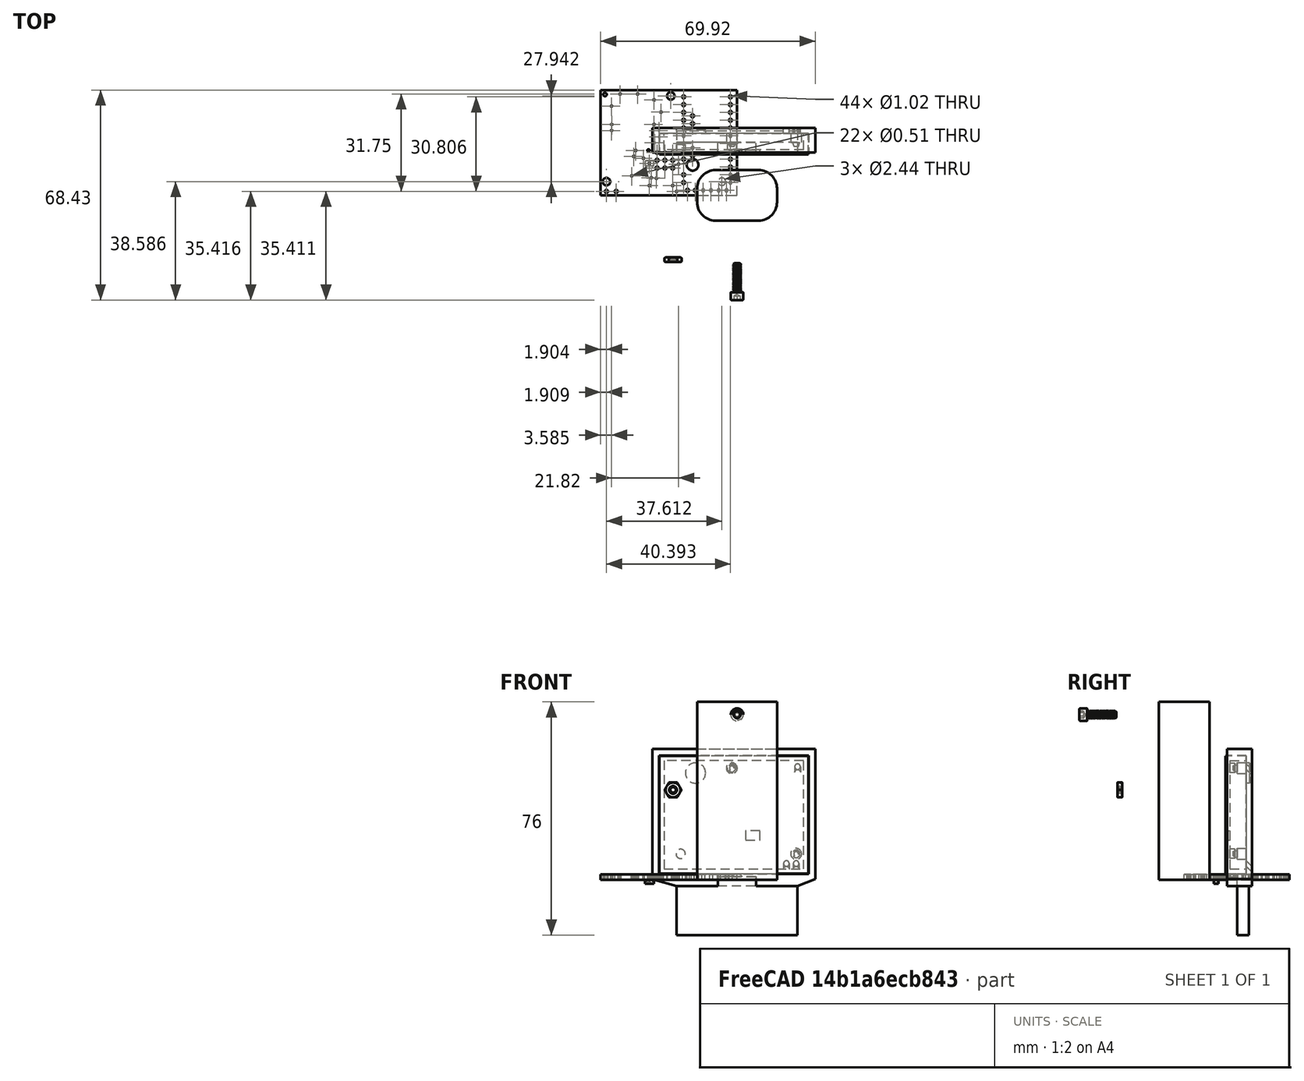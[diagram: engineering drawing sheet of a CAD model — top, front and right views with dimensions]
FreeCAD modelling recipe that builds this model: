
FCSTD DOCUMENT  (FreeCAD 1.0R39109 (Git))
Label: Placement
License: All rights reserved
LicenseURL: https://en.wikipedia.org/wiki/All_rights_reserved
objects: Sketcher::SketchObject×17, PartDesign::Pad×11, PartDesign::Point×11, PartDesign::Plane×6, Part::Feature×5, PartDesign::Pocket×5, PartDesign::SubShapeBinder×4, Mesh::Feature×4, App::Part×3, PartDesign::Body×3
note: 111 computed .brp shape members not serialized (recipe doc carries the construction recipe); baked Part::Feature solids carry a one-line shape summary decoded from their .brp

FEATURE [Part::Feature] Part__Feature006  label="pcb"
  Placement = pos=(0,0,0) rot=(0,0,1;1.5708rad)
  shape: bbox 44.45 x 34.29 x 1.778 mm, 78 faces (baked)
FEATURE [Part::Feature] Part__Feature007  label="SOT23"
  Placement = pos=(-28.5698,10.3914,0) rot=(0,1,0;3.14159rad)
  shape: bbox 2.9 x 2.134 x 1.25 mm, 27 faces (baked)
FEATURE [App::Part] pcb  label="pcb001"
  Group = -> [Part__Feature006,Part__Feature007]
  Origin = -> Origin001
  Placement = pos=(-23.3,15.5,4) rot=(0,0.707107,0.707107;3.14159rad)
FEATURE [Sketcher::SketchObject] Sketch
  ArcFitTolerance = 1e-06
  AttachmentSupport = -> [XY_Plane003]
  FullyConstrained = true
  MakeInternals = false
  MapMode = 5
  sketch-geometry (13):
    g0: LineSegment StartX=13 StartY=-2.25 StartZ=0 EndX=13 EndY=2.25 EndZ=0
    g1: LineSegment StartX=7 StartY=8.25 StartZ=0 EndX=-7 EndY=8.25 EndZ=0
    g2: LineSegment StartX=-13 StartY=2.25 StartZ=0 EndX=-13 EndY=-2.25 EndZ=0
    g3: LineSegment StartX=-7 StartY=-8.25 StartZ=0 EndX=7 EndY=-8.25 EndZ=0
    g4: GeomPoint [constr] X=0 Y=0 Z=0
    g5: ArcOfCircle CenterX=-7 CenterY=2.25 CenterZ=0 NormalX=0 NormalY=0 NormalZ=1 AngleXU=0 Radius=6 StartAngle=1.5708 EndAngle=3.14159
    g6: GeomPoint [constr] X=-13 Y=8.25 Z=0
    g7: ArcOfCircle CenterX=7 CenterY=2.25 CenterZ=0 NormalX=0 NormalY=0 NormalZ=1 AngleXU=0 Radius=6 StartAngle=7e-15 EndAngle=1.5708
    g8: GeomPoint [constr] X=13 Y=8.25 Z=0
    g9: ArcOfCircle CenterX=7 CenterY=-2.25 CenterZ=0 NormalX=0 NormalY=0 NormalZ=1 AngleXU=0 Radius=6 StartAngle=4.71239 EndAngle=6.28319
    g10: GeomPoint [constr] X=13 Y=-8.25 Z=0
    g11: ArcOfCircle CenterX=-7 CenterY=-2.25 CenterZ=0 NormalX=0 NormalY=0 NormalZ=1 AngleXU=0 Radius=6 StartAngle=3.14159 EndAngle=4.71239
    g12: GeomPoint [constr] X=-13 Y=-8.25 Z=0
  constraints (28):
    c: Vertical(g0)
    c: Vertical(g2)
    c: Horizontal(g1)
    c: Horizontal(g3)
    c: Symmetric(g6,g10,g4)
    c: Coincident(g4,g-1)
    c: DistanceY(g12,g6) = 16.5
    c: DistanceX(g6,g8) = 26
    c: PointOnObject(g6,g1)
    c: PointOnObject(g6,g2)
    c: Tangent(g1,g5) = -1.5708
    c: Tangent(g2,g5) = -1.5708
    c: PointOnObject(g8,g1)
    c: PointOnObject(g8,g0)
    c: Tangent(g1,g7) = -1.5708
    c: Tangent(g0,g7) = -1.5708
    c: PointOnObject(g10,g0)
    c: PointOnObject(g10,g3)
    c: Tangent(g0,g9) = -1.5708
    c: Tangent(g3,g9) = -1.5708
    c: PointOnObject(g12,g3)
    c: PointOnObject(g12,g2)
    c: Tangent(g3,g11) = -1.5708
    c: Tangent(g2,g11) = -1.5708
    c: Equal(g5,g11)
    c: Equal(g11,g9)
    c: Equal(g11,g7)
    c: Radius(g7) = 6
FEATURE [PartDesign::Pad] Pad
  Direction = (0,0,1)
  Length = 58
  Length2 = 10
  Profile = -> Sketch
  ReferenceAxis = -> Sketch [N_Axis]
  Refine = true
  Suppressed = false
  Type = 0
FEATURE [PartDesign::Body] Body
  AllowCompound = false
  Group = -> [Sketch,Pad]
  Origin = -> Origin003
  Tip = -> Pad
FEATURE [App::Part] Part001  label="AA holder"
  Group = -> [Body]
  Origin = -> Origin002
  Placement = pos=(0,-35.5,-12) rot=(0,0,1;0rad)
FEATURE [Part::Feature] Part__Feature  label="Num 3 socket head"
  Placement = pos=(0,-22.098,53.848) rot=(1,0,0;1.5708rad)
  shape: bbox 4.09 x 12.24 x 4.09 mm, 70 faces (baked)
FEATURE [Part::Feature] Part__Feature008  label="num 3 nut"
  Placement = pos=(-20.85,-21,29.3) rot=(0,1,0;0.523599rad)
  shape: bbox 5.5 x 2.051 x 5.5 mm, 38 faces (baked)
FEATURE [PartDesign::SubShapeBinder] Binder
  BindCopyOnChange = 0
  BindMode = 0
  ClaimChildren = false
  Context = -> Part [Body001.Binder.]
  Fuse = false
  MakeFace = true
  OffsetFill = false
  OffsetIntersection = false
  OffsetJoinType = 0
  OffsetOpenResult = false
  PartialLoad = false
  Refine = true
  Relative = true
  Support = -> [pcb[Part__Feature006.]]
  _Version = 2
FEATURE [PartDesign::SubShapeBinder] Binder001
  BindCopyOnChange = 0
  BindMode = 0
  ClaimChildren = false
  Context = -> Part [Body001.Binder001.]
  Fuse = false
  MakeFace = true
  OffsetFill = false
  OffsetIntersection = false
  OffsetJoinType = 0
  OffsetOpenResult = false
  PartialLoad = false
  Refine = true
  Relative = true
  Support = -> [pcb[Part__Feature007.]]
  _Version = 2
FEATURE [PartDesign::Plane] DatumPlane  label="enclosure face PCB"
  AttachmentOffset = pos=(0,0,0.635) rot=(0,0,1;0rad)
  AttachmentSupport = -> [Binder]
  Length = 61.8227
  MapMode = 5
  Placement = pos=(0,14.865,1e-16) rot=(1,0,0;1.5708rad)
  ResizeMode = 0
  Width = 76.8127
FEATURE [PartDesign::Plane] DatumPlane001  label="sensor face"
  AttachmentSupport = -> [Binder001]
  Length = 76.8127
  MapMode = 11
  Placement = pos=(5.26981,14.25,14.3914) rot=(0.57735,0.57735,0.57735;4.18879rad)
  ResizeMode = 0
  Width = 61.8227
FEATURE [Sketcher::SketchObject] Sketch001
  ArcFitTolerance = 1e-06
  AttachmentSupport = -> [DatumPlane]
  ExternalGeometry = -> [Binder]
  FullyConstrained = true
  MakeInternals = false
  MapMode = 5
  Placement = pos=(0,14.865,1e-16) rot=(1,0,0;1.5708rad)
  sketch-geometry (4):
    g0: LineSegment StartX=-25.332 StartY=40.322 StartZ=0 EndX=-25.332 EndY=1.968 EndZ=0
    g1: LineSegment StartX=-25.332 StartY=1.968 StartZ=0 EndX=23.182 EndY=1.968 EndZ=0
    g2: LineSegment StartX=23.182 StartY=1.968 StartZ=0 EndX=23.182 EndY=40.322 EndZ=0
    g3: LineSegment StartX=23.182 StartY=40.322 StartZ=0 EndX=-25.332 EndY=40.322 EndZ=0
  constraints (12):
    c: Coincident(g0,g1)
    c: Coincident(g1,g2)
    c: Coincident(g2,g3)
    c: Coincident(g3,g0)
    c: Vertical(g0)
    c: Vertical(g2)
    c: Horizontal(g1)
    c: Horizontal(g3)
    c: DistanceX(g0,g-3) = 2.032
    c: DistanceX(g-3,g2) = 2.032
    c: DistanceY(g0,g-4) = 2.032
    c: DistanceY(g-3,g2) = 2.032
FEATURE [PartDesign::Pad] Pad001
  Direction = (0,-1,2e-16)
  Length = 1.50012
  Length2 = 10
  Placement = pos=(1.3e-15,14.865,3.6e-15) rot=(1,0,0;1.5708rad)
  Profile = -> Sketch001
  ReferenceAxis = -> Sketch001 [N_Axis]
  Refine = true
  Suppressed = false
  Type = 0
FEATURE [Sketcher::SketchObject] Sketch002
  ArcFitTolerance = 1e-06
  AttachmentSupport = -> [DatumPlane001]
  ExternalGeometry = -> [Binder001]
  FullyConstrained = false
  MakeInternals = false
  MapMode = 5
  Placement = pos=(5.26981,14.25,14.3914) rot=(0.57735,0.57735,0.57735;4.18879rad)
  sketch-geometry (4):
    g0: LineSegment StartX=-1.49114 StartY=2.17791 StartZ=0 EndX=-1.49114 EndY=-2.49451 EndZ=0
    g1: LineSegment StartX=-1.49114 StartY=-2.49451 StartZ=0 EndX=1.64977 EndY=-2.49451 EndZ=0
    g2: LineSegment StartX=1.64977 StartY=-2.49451 StartZ=0 EndX=1.64977 EndY=2.17791 EndZ=0
    g3: LineSegment StartX=1.64977 StartY=2.17791 StartZ=0 EndX=-1.49114 EndY=2.17791 EndZ=0
  constraints (8):
    c: Coincident(g0,g1)
    c: Coincident(g1,g2)
    c: Coincident(g2,g3)
    c: Coincident(g3,g0)
    c: Vertical(g0)
    c: Vertical(g2)
    c: Horizontal(g1)
    c: Horizontal(g3)
FEATURE [PartDesign::Pocket] Pocket
  BaseFeature = -> Pad001
  Direction = (0,-1,0)
  Length = 5
  Length2 = 5
  Placement = pos=(1.3e-15,14.865,3.6e-15) rot=(1,0,0;1.5708rad)
  Profile = -> Sketch002
  ReferenceAxis = -> Sketch002 [N_Axis]
  Refine = true
  Reversed = true
  Suppressed = false
  Type = 1
FEATURE [Sketcher::SketchObject] Sketch003
  ArcFitTolerance = 1e-06
  AttachmentSupport = -> [DatumPlane]
  ExternalGeometry = -> [Pocket]
  FullyConstrained = true
  MakeInternals = false
  MapMode = 5
  Placement = pos=(0,14.865,1e-16) rot=(1,0,0;1.5708rad)
  sketch-geometry (10):
    g0: LineSegment StartX=23.182 StartY=40.322 StartZ=0 EndX=-25.332 EndY=40.322 EndZ=0
    g1: LineSegment StartX=-25.332 StartY=40.322 StartZ=0 EndX=-25.332 EndY=1.968 EndZ=0
    g2: LineSegment StartX=-25.332 StartY=1.968 StartZ=0 EndX=23.182 EndY=1.968 EndZ=0
    g3: LineSegment StartX=23.182 StartY=1.968 StartZ=0 EndX=23.182 EndY=40.322 EndZ=0
    g4: LineSegment StartX=21.658 StartY=38.798 StartZ=0 EndX=-23.808 EndY=38.798 EndZ=0
    g5: LineSegment StartX=-23.808 StartY=38.798 StartZ=0 EndX=-23.808 EndY=3.492 EndZ=0
    g6: LineSegment StartX=-23.808 StartY=3.492 StartZ=0 EndX=21.658 EndY=3.492 EndZ=0
    g7: LineSegment StartX=21.658 StartY=3.492 StartZ=0 EndX=21.658 EndY=38.798 EndZ=0
    g8: LineSegment [constr] StartX=-1.075 StartY=38.798 StartZ=0 EndX=-1.075 EndY=40.322 EndZ=0
    g9: LineSegment [constr] StartX=21.658 StartY=21.145 StartZ=0 EndX=23.182 EndY=21.145 EndZ=0
  constraints (26):
    c: Coincident(g0,g1)
    c: Coincident(g1,g2)
    c: Coincident(g2,g3)
    c: Coincident(g3,g0)
    c: Horizontal(g0)
    c: Horizontal(g2)
    c: Vertical(g1)
    c: Vertical(g3)
    c: Coincident(g0,g-3)
    c: Coincident(g1,g-4)
    c: Coincident(g4,g5)
    c: Coincident(g5,g6)
    c: Coincident(g6,g7)
    c: Coincident(g7,g4)
    c: Horizontal(g4)
    c: Horizontal(g6)
    c: Vertical(g5)
    c: Vertical(g7)
    c: Symmetric(g4,g4,g8)
    c: Symmetric(g0,g0,g8)
    c: Vertical(g8)
    c: Symmetric(g7,g7,g9)
    c: Symmetric(g3,g3,g9)
    c: Horizontal(g9)
    c: Equal(g9,g8)
    c: DistanceY(g8,g8) = 1.524
FEATURE [PartDesign::Pad] Pad002
  BaseFeature = -> Pocket
  Direction = (0,-1,2e-16)
  Length = 5.334
  Length2 = 10
  Placement = pos=(1.3e-15,14.865,3.6e-15) rot=(1,0,0;1.5708rad)
  Profile = -> Sketch003
  ReferenceAxis = -> Sketch003 [N_Axis]
  Refine = true
  Reversed = true
  Suppressed = false
  Type = 0
FEATURE [Part::Feature] Pluviometer_base_pts
  shape: bbox 120 x 120 x 80 mm, 0 faces, 0 solids (baked)
FEATURE [PartDesign::Plane] DatumPlane002
  AttachmentSupport = -> [Pluviometer_base_pts]
  Length = 65.0694
  MapMode = 13
  Placement = pos=(6.66667,21,-7.33333) rot=(0,0.707107,0.707107;3.14159rad)
  ResizeMode = 0
  Width = 79.6104
FEATURE [PartDesign::Point] DatumPoint
  AttacherType = Attacher::AttachEnginePoint
  AttachmentSupport = -> [Pluviometer_base_pts]
  MapMode = 37
  Placement = pos=(20,17,-18) rot=(0,0,1;0rad)
FEATURE [PartDesign::Point] DatumPoint001
  AttacherType = Attacher::AttachEnginePoint
  AttachmentSupport = -> [Pluviometer_base_pts]
  MapMode = 37
  Placement = pos=(20,17,-18) rot=(0,0,1;0rad)
FEATURE [PartDesign::Point] DatumPoint002
  AttacherType = Attacher::AttachEnginePoint
  AttachmentSupport = -> [Pluviometer_base_pts]
  MapMode = 37
  Placement = pos=(-20,17,-18) rot=(0,0,1;0rad)
FEATURE [PartDesign::Point] DatumPoint003
  AttacherType = Attacher::AttachEnginePoint
  AttachmentSupport = -> [Pluviometer_base_pts]
  MapMode = 37
  Placement = pos=(-20,21,-2) rot=(0,0,1;0rad)
FEATURE [PartDesign::Point] DatumPoint004
  AttacherType = Attacher::AttachEnginePoint
  AttachmentSupport = -> [Pluviometer_base_pts]
  MapMode = 37
  Placement = pos=(-20,21,-2) rot=(0,0,1;0rad)
FEATURE [PartDesign::Point] DatumPoint005
  AttacherType = Attacher::AttachEnginePoint
  AttachmentSupport = -> [Pluviometer_base_pts]
  MapMode = 37
  Placement = pos=(20,21,-2) rot=(0,0,1;0rad)
FEATURE [Sketcher::SketchObject] Sketch004
  ArcFitTolerance = 1e-06
  AttachmentSupport = -> [DatumPlane002]
  ExternalGeometry = -> [DatumPoint005,DatumPoint003,DatumPoint002,DatumPoint]
  FullyConstrained = true
  MakeInternals = false
  MapMode = 5
  Placement = pos=(6.66667,21,-7.33333) rot=(0,0.707107,0.707107;3.14159rad)
  sketch-geometry (4):
    g0: LineSegment StartX=-13.0333 StartY=5.33333 StartZ=0 EndX=-13.0333 EndY=-10.6667 EndZ=0
    g1: LineSegment StartX=-13.0333 StartY=-10.6667 StartZ=0 EndX=26.3667 EndY=-10.6667 EndZ=0
    g2: LineSegment StartX=26.3667 StartY=-10.6667 StartZ=0 EndX=26.3667 EndY=5.33333 EndZ=0
    g3: LineSegment StartX=26.3667 StartY=5.33333 StartZ=0 EndX=-13.0333 EndY=5.33333 EndZ=0
  constraints (12):
    c: Coincident(g0,g1)
    c: Coincident(g1,g2)
    c: Coincident(g2,g3)
    c: Coincident(g3,g0)
    c: Vertical(g0)
    c: Vertical(g2)
    c: Horizontal(g1)
    c: Horizontal(g3)
    c: Horizontal(g0,g-3)
    c: Horizontal(g-6,g0)
    c: DistanceX(g-3,g0) = 0.3
    c: DistanceX(g2,g-4) = 0.3
FEATURE [PartDesign::Pad] Pad003
  Direction = (0,1,-2e-16)
  Length = 3.75
  Length2 = 10
  Placement = pos=(6.66667,21,-7.33333) rot=(0,0.707107,0.707107;3.14159rad)
  Profile = -> Sketch004
  ReferenceAxis = -> Sketch004 [N_Axis]
  Refine = true
  Reversed = true
  Suppressed = false
  Type = 0
FEATURE [PartDesign::SubShapeBinder] Binder002
  BindCopyOnChange = 0
  BindMode = 0
  ClaimChildren = false
  Context = -> Part [Body002.Binder002.]
  Fuse = false
  MakeFace = true
  OffsetFill = false
  OffsetIntersection = false
  OffsetJoinType = 0
  OffsetOpenResult = false
  PartialLoad = false
  Refine = true
  Relative = true
  Support = -> [Body001]
  _Version = 2
FEATURE [Sketcher::SketchObject] Sketch005
  ArcFitTolerance = 1e-06
  AttachmentSupport = -> [DatumPlane002]
  ExternalGeometry = -> [Binder002,Pad003]
  FullyConstrained = false
  MakeInternals = false
  MapMode = 5
  Placement = pos=(6.66667,21,-7.33333) rot=(0,0.707107,0.707107;3.14159rad)
  sketch-geometry (8):
    g0: LineSegment StartX=-13.0333 StartY=5.33333 StartZ=0 EndX=-13.0333 EndY=-10.6667 EndZ=0
    g1: LineSegment StartX=-13.0333 StartY=-10.6667 StartZ=0 EndX=26.3667 EndY=-10.6667 EndZ=0
    g2: LineSegment StartX=26.3667 StartY=-10.6667 StartZ=0 EndX=26.3667 EndY=5.33333 EndZ=0
    g3: LineSegment StartX=-18.8013 StartY=49.9413 StartZ=0 EndX=-18.8013 EndY=7.52333 EndZ=0
    g4: LineSegment StartX=34.2847 StartY=7.52333 StartZ=0 EndX=34.2847 EndY=49.9413 EndZ=0
    g5: LineSegment StartX=34.2847 StartY=49.9413 StartZ=0 EndX=-18.8013 EndY=49.9413 EndZ=0
    g6: LineSegment StartX=-13.0333 StartY=5.33333 StartZ=0 EndX=-18.8013 EndY=7.52333 EndZ=0
    g7: LineSegment StartX=26.3667 StartY=5.33333 StartZ=0 EndX=34.2847 EndY=7.52333 EndZ=0
  constraints (18):
    c: Coincident(g0,g-6)
    c: Vertical(g0)
    c: Coincident(g1,g0)
    c: Coincident(g1,g-6)
    c: Coincident(g2,g1)
    c: Coincident(g4,g5)
    c: Coincident(g5,g3)
    c: Vertical(g3)
    c: Vertical(g4)
    c: Horizontal(g5)
    c: DistanceX(g3,g-3) = 2.286
    c: DistanceX(g-3,g4) = 2.286
    c: DistanceY(g-3,g3) = 2.286
    c: DistanceY(g3,g-4) = 1.778
    c: Coincident(g6,g0)
    c: Coincident(g6,g3)
    c: Coincident(g7,g2)
    c: Coincident(g7,g4)
FEATURE [PartDesign::Plane] DatumPlane003
  AttachmentSupport = -> [Binder002]
  Length = 65.0694
  MapMode = 13
  Placement = pos=(6.50267,20.199,15.2607) rot=(1,0,0;1.5708rad)
  ResizeMode = 0
  Width = 79.6104
FEATURE [PartDesign::Pad] Pad004
  BaseFeature = -> Pad003
  Direction = (0,1,-2e-16)
  Length = 10
  Length2 = 10
  Placement = pos=(6.66667,21,-7.33333) rot=(0,0.707107,0.707107;3.14159rad)
  Profile = -> Sketch005
  ReferenceAxis = -> Sketch005 [N_Axis]
  Refine = true
  Suppressed = false
  Type = 3
  UpToFace = -> DatumPlane003
FEATURE [Sketcher::SketchObject] Sketch006
  ArcFitTolerance = 1e-06
  AttachmentSupport = -> [Pad004]
  ExternalGeometry = -> [Binder002,Pad004]
  FullyConstrained = true
  MakeInternals = false
  MapMode = 5
  Placement = pos=(6.66667,20.199,-7.33333) rot=(0,0.707107,-0.707107;3.14159rad)
  sketch-geometry (10):
    g0: LineSegment StartX=-16.6423 StartY=-9.17433 StartZ=0 EndX=-16.6423 EndY=-47.7823 EndZ=0
    g1: LineSegment StartX=-16.6423 StartY=-47.7823 StartZ=0 EndX=32.1257 EndY=-47.7823 EndZ=0
    g2: LineSegment StartX=32.1257 StartY=-47.7823 StartZ=0 EndX=32.1257 EndY=-9.17433 EndZ=0
    g3: LineSegment StartX=32.1257 StartY=-9.17433 StartZ=0 EndX=-16.6423 EndY=-9.17433 EndZ=0
    g4: LineSegment StartX=34.2847 StartY=-7.52333 StartZ=0 EndX=34.2847 EndY=-49.9413 EndZ=0
    g5: LineSegment StartX=34.2847 StartY=-49.9413 StartZ=0 EndX=-18.8013 EndY=-49.9413 EndZ=0
    g6: LineSegment StartX=-18.8013 StartY=-49.9413 StartZ=0 EndX=-18.8013 EndY=-7.52333 EndZ=0
    g7: LineSegment StartX=-18.8013 StartY=-7.52333 StartZ=0 EndX=-13.0333 EndY=-5.33333 EndZ=0
    g8: LineSegment StartX=-13.0333 StartY=-5.33333 StartZ=0 EndX=26.3667 EndY=-5.33333 EndZ=0
    g9: LineSegment StartX=26.3667 StartY=-5.33333 StartZ=0 EndX=34.2847 EndY=-7.52333 EndZ=0
  constraints (24):
    c: Coincident(g0,g1)
    c: Coincident(g1,g2)
    c: Coincident(g2,g3)
    c: Coincident(g3,g0)
    c: Vertical(g0)
    c: Vertical(g2)
    c: Horizontal(g1)
    c: Horizontal(g3)
    c: DistanceX(g0,g-3) = 0.127
    c: DistanceX(g-3,g2) = 0.127
    c: DistanceY(g-3,g2) = 0.127
    c: DistanceY(g1,g-4) = 0.127
    c: Coincident(g4,g-8)
    c: Coincident(g4,g-5)
    c: Coincident(g5,g4)
    c: Coincident(g5,g-5)
    c: Coincident(g6,g5)
    c: Coincident(g6,g-9)
    c: Coincident(g7,g-9)
    c: Coincident(g7,g-6)
    c: Coincident(g8,g-6)
    c: Coincident(g8,g-7)
    c: Coincident(g9,g-7)
    c: Coincident(g9,g4)
FEATURE [Sketcher::SketchObject] Sketch009
  ArcFitTolerance = 1e-06
  AttachmentSupport = -> [Pad002]
  ExternalGeometry = -> [Binder]
  FullyConstrained = true
  MakeInternals = false
  MapMode = 5
  Placement = pos=(1.3e-15,14.865,3.6e-15) rot=(-1,0,0;1.5708rad)
  sketch-geometry (2):
    g0: Circle CenterX=-18.3663 CenterY=-8.44604 CenterZ=0 NormalX=0 NormalY=0 NormalZ=1 AngleXU=0 Radius=1.524
    g1: Circle CenterX=-1.71311 CenterY=-36.3881 CenterZ=0 NormalX=0 NormalY=0 NormalZ=1 AngleXU=0 Radius=1.524
  constraints (4):
    c: Coincident(g0,g-3)
    c: Coincident(g1,g-4)
    c: Diameter(g1) = 3.048
    c: Equal(g0,g1)
FEATURE [PartDesign::Pad] Pad007
  BaseFeature = -> Pad002
  Direction = (0,1,2e-16)
  Length = 1.5875
  Length2 = 10
  Placement = pos=(1.3e-15,14.865,3.6e-15) rot=(1,0,0;1.5708rad)
  Profile = -> Sketch009
  ReferenceAxis = -> Sketch009 [N_Axis]
  Refine = true
  Suppressed = false
  Type = 3
  UpToFace = -> Binder [Face75]
FEATURE [PartDesign::Body] Body001
  AllowCompound = false
  Group = -> [Binder,Binder001,DatumPlane,DatumPlane001,Sketch001,Pad001,Sketch002,Pocket,Sketch003,Pad002,Sketch009,Pad007]
  Origin = -> Origin004
  Tip = -> Pad007
FEATURE [Mesh::Feature] Pluviometer_funnel  label="Pluviometer-funnel"
FEATURE [Mesh::Feature] Pluviometer_AA  label="Pluviometer-AA"
FEATURE [Mesh::Feature] Pluviometer_base  label="Pluviometer-base"
FEATURE [PartDesign::SubShapeBinder] Binder003
  BindCopyOnChange = 0
  BindMode = 0
  ClaimChildren = false
  Context = -> Part [Body002.Binder003.]
  Fuse = false
  MakeFace = true
  OffsetFill = false
  OffsetIntersection = false
  OffsetJoinType = 0
  OffsetOpenResult = false
  PartialLoad = false
  Refine = true
  Relative = true
  Support = -> [pcb]
  _Version = 2
FEATURE [PartDesign::Point] DatumPoint006
  AttacherType = Attacher::AttachEnginePoint
  AttachmentSupport = -> [Pluviometer_base_pts]
  MapMode = 37
  Placement = pos=(6,17,1) rot=(0,0,1;0rad)
FEATURE [PartDesign::Point] DatumPoint007
  AttacherType = Attacher::AttachEnginePoint
  AttachmentSupport = -> [Pluviometer_base_pts]
  MapMode = 37
  Placement = pos=(-6,17,1) rot=(0,0,1;0rad)
FEATURE [PartDesign::Plane] DatumPlane004  label="axle end"
  AttachmentSupport = -> [Pluviometer_base_pts]
  Length = 65.0694
  MapMode = 13
  Placement = pos=(0.362446,15,-0.177299) rot=(0,0.707107,0.707107;3.14159rad)
  ResizeMode = 0
  Width = 79.6104
FEATURE [PartDesign::Point] DatumPoint008  label="axle end circle 1"
  AttacherType = Attacher::AttachEnginePoint
  AttachmentSupport = -> [Pluviometer_base_pts]
  MapMode = 37
  Placement = pos=(1.625,15,0) rot=(0,0,1;0rad)
FEATURE [PartDesign::Point] DatumPoint009  label="axle end circle 2"
  AttacherType = Attacher::AttachEnginePoint
  AttachmentSupport = -> [Pluviometer_base_pts]
  MapMode = 37
  Placement = pos=(-1.625,-15,0) rot=(0,0,1;0rad)
FEATURE [PartDesign::Point] DatumPoint010  label="axle end circle 3"
  AttacherType = Attacher::AttachEnginePoint
  AttachmentSupport = -> [Pluviometer_base_pts]
  MapMode = 37
  Placement = pos=(-0.8125,15,-1.40729) rot=(0,0,1;0rad)
FEATURE [Mesh::Feature] Pluviometer_bucket  label="Pluviometer-bucket"
  Placement = pos=(0,0,0) rot=(0,1,0;0.349066rad)
FEATURE [Sketcher::SketchObject] Sketch014
  ArcFitTolerance = 1e-06
  AttachmentSupport = -> [DatumPlane002]
  ExternalGeometry = -> [Pad004,Sketch005]
  FullyConstrained = true
  MakeInternals = false
  MapMode = 5
  Placement = pos=(6.66667,21,-7.33333) rot=(0,0.707107,0.707107;3.14159rad)
  sketch-geometry (7):
    g0: LineSegment StartX=34.2847 StartY=7.52333 StartZ=0 EndX=34.2847 EndY=49.9413 EndZ=0
    g1: LineSegment StartX=34.2847 StartY=49.9413 StartZ=0 EndX=-18.8013 EndY=49.9413 EndZ=0
    g2: LineSegment StartX=-18.8013 StartY=49.9413 StartZ=0 EndX=-18.8013 EndY=7.52333 EndZ=0
    g3: LineSegment [constr] StartX=-18.8013 StartY=7.52333 StartZ=0 EndX=34.2847 EndY=7.52333 EndZ=0
    g4: LineSegment StartX=-18.8013 StartY=7.52333 StartZ=0 EndX=-13.0333 EndY=5.33333 EndZ=0
    g5: LineSegment StartX=-13.0333 StartY=5.33333 StartZ=0 EndX=26.3667 EndY=5.33333 EndZ=0
    g6: LineSegment StartX=26.3667 StartY=5.33333 StartZ=0 EndX=34.2847 EndY=7.52333 EndZ=0
  constraints (16):
    c: Coincident(g0,g1)
    c: Coincident(g1,g2)
    c: Coincident(g2,g3)
    c: Coincident(g3,g0)
    c: Vertical(g0)
    c: Vertical(g2)
    c: Horizontal(g1)
    c: Horizontal(g3)
    c: Coincident(g0,g-3)
    c: Coincident(g1,g-4)
    c: Coincident(g4,g2)
    c: Coincident(g4,g-5)
    c: Coincident(g5,g4)
    c: Coincident(g5,g-6)
    c: Coincident(g6,g5)
    c: Coincident(g6,g0)
FEATURE [PartDesign::Pad] Pad008
  BaseFeature = -> Pad004
  Direction = (0,1,-2e-16)
  Length = 1.016
  Length2 = 10
  Placement = pos=(6.66667,21,-7.33333) rot=(0,0.707107,0.707107;3.14159rad)
  Profile = -> Sketch014
  ReferenceAxis = -> Sketch014 [N_Axis]
  Refine = true
  Suppressed = false
  Type = 0
FEATURE [PartDesign::Pad] Pad005
  BaseFeature = -> Pad008
  Direction = (0,-1,-2e-16)
  Length = 2
  Length2 = 10
  Placement = pos=(6.66667,21,-7.33333) rot=(0,0.707107,0.707107;3.14159rad)
  Profile = -> Sketch006
  ReferenceAxis = -> Sketch006 [N_Axis]
  Refine = true
  Suppressed = false
  Type = 3
  UpToFace = -> Pad004 [Face1]
FEATURE [Sketcher::SketchObject] Sketch007
  ArcFitTolerance = 1e-06
  AttachmentSupport = -> [Pad005]
  FullyConstrained = false
  MakeInternals = false
  MapMode = 5
  Placement = pos=(6.66667,21,-7.33333) rot=(0,0.707107,0.707107;3.14159rad)
  sketch-geometry (4):
    g0: LineSegment StartX=9.95147 StartY=11.0285 StartZ=0 EndX=30.2715 EndY=11.0285 EndZ=0
    g1: LineSegment StartX=30.2715 StartY=11.0285 StartZ=0 EndX=30.2715 EndY=17.4643 EndZ=0
    g2: LineSegment StartX=30.2715 StartY=17.4643 StartZ=0 EndX=9.95147 EndY=17.4643 EndZ=0
    g3: LineSegment StartX=9.95147 StartY=17.4643 StartZ=0 EndX=9.95147 EndY=11.0285 EndZ=0
  constraints (10):
    c: Coincident(g0,g1)
    c: Coincident(g1,g2)
    c: Coincident(g2,g3)
    c: Coincident(g3,g0)
    c: Horizontal(g0)
    c: Horizontal(g2)
    c: Vertical(g1)
    c: Vertical(g3)
    c: Distance(g1,g3) = 20.32
    c: Coincident(g0,g-3)
FEATURE [Sketcher::SketchObject] Sketch008
  ArcFitTolerance = 1e-06
  ExternalGeometry = -> [Pad005]
  FullyConstrained = true
  MakeInternals = false
  MapMode = 5
  Placement = pos=(6.66667,17.25,-7.33333) rot=(0,0.707107,-0.707107;3.14159rad)
  sketch-geometry (10):
    g0: LineSegment StartX=-13.0333 StartY=-5.33333 StartZ=0 EndX=26.3667 EndY=-5.33333 EndZ=0
    g1: LineSegment StartX=26.3667 StartY=-5.33333 StartZ=0 EndX=34.2847 EndY=-7.52333 EndZ=0
    g2: LineSegment StartX=34.2847 StartY=-7.52333 StartZ=0 EndX=34.2847 EndY=-49.9413 EndZ=0
    g3: LineSegment StartX=34.2847 StartY=-49.9413 StartZ=0 EndX=-18.8013 EndY=-49.9413 EndZ=0
    g4: LineSegment StartX=-18.8013 StartY=-49.9413 StartZ=0 EndX=-18.8013 EndY=-7.52333 EndZ=0
    g5: LineSegment StartX=-18.8013 StartY=-7.52333 StartZ=0 EndX=-13.0333 EndY=-5.33333 EndZ=0
    g6: LineSegment StartX=-16.6423 StartY=-9.17433 StartZ=0 EndX=32.1257 EndY=-9.17433 EndZ=0
    g7: LineSegment StartX=32.1257 StartY=-9.17433 StartZ=0 EndX=32.1257 EndY=-47.7823 EndZ=0
    g8: LineSegment StartX=32.1257 StartY=-47.7823 StartZ=0 EndX=-16.6423 EndY=-47.7823 EndZ=0
    g9: LineSegment StartX=-16.6423 StartY=-47.7823 StartZ=0 EndX=-16.6423 EndY=-9.17433 EndZ=0
  constraints (20):
    c: Coincident(g0,g-3)
    c: Coincident(g0,g-4)
    c: Coincident(g1,g0)
    c: Coincident(g1,g-4)
    c: Coincident(g2,g1)
    c: Coincident(g2,g-7)
    c: Coincident(g3,g2)
    c: Coincident(g3,g-7)
    c: Coincident(g4,g3)
    c: Coincident(g4,g-3)
    c: Coincident(g5,g4)
    c: Coincident(g5,g0)
    c: Coincident(g6,g-5)
    c: Coincident(g6,g-5)
    c: Coincident(g7,g6)
    c: Coincident(g7,g-6)
    c: Coincident(g8,g7)
    c: Coincident(g8,g-6)
    c: Coincident(g9,g8)
    c: Coincident(g9,g6)
FEATURE [PartDesign::Pad] Pad006
  BaseFeature = -> Pad005
  Direction = (1e-16,-1,-2e-16)
  Length = 3.302
  Length2 = 10
  Placement = pos=(6.66667,21,-7.33333) rot=(0,0.707107,0.707107;3.14159rad)
  Profile = -> Sketch008
  ReferenceAxis = -> Sketch008 [N_Axis]
  Refine = true
  Suppressed = false
  Type = 0
FEATURE [Sketcher::SketchObject] Sketch011
  ArcFitTolerance = 1e-06
  AttachmentSupport = -> [Pad006]
  ExternalGeometry = -> [Binder003]
  FullyConstrained = true
  MakeInternals = false
  MapMode = 5
  Placement = pos=(6.66667,20.199,-7.33333) rot=(0,0.707107,-0.707107;3.14159rad)
  sketch-geometry (3):
    g0: Circle CenterX=-13.0515 CenterY=-44.1987 CenterZ=0 NormalX=0 NormalY=0 NormalZ=1 AngleXU=0 Radius=0.9144
    g1: Circle CenterX=-12.5742 CenterY=-12.6096 CenterZ=0 NormalX=0 NormalY=0 NormalZ=1 AngleXU=0 Radius=0.9144
    g2: Circle CenterX=-9.39918 CenterY=-12.6096 CenterZ=0 NormalX=0 NormalY=0 NormalZ=1 AngleXU=0 Radius=0.9144
  constraints (6):
    c: Coincident(g0,g-5)
    c: Coincident(g1,g-4)
    c: Coincident(g2,g-3)
    c: Diameter(g1) = 1.8288
    c: Equal(g1,g2)
    c: Equal(g2,g0)
FEATURE [PartDesign::Pocket] Pocket003
  BaseFeature = -> Pad006
  Direction = (0,1,-1)
  Length = 5
  Length2 = 5
  Placement = pos=(6.66667,21,-7.33333) rot=(0,0.707107,0.707107;3.14159rad)
  Profile = -> Sketch011
  ReferenceAxis = -> Sketch011 [N_Axis]
  Refine = true
  Suppressed = false
  Type = 1
  UseCustomVector = true
FEATURE [Sketcher::SketchObject] Sketch012
  ArcFitTolerance = 1e-06
  AttachmentSupport = -> [Pocket003]
  ExternalGeometry = -> [DatumPoint006,DatumPoint007,Pocket003]
  FullyConstrained = true
  MakeInternals = false
  MapMode = 5
  Placement = pos=(6.66667,13.948,-7.33333) rot=(0,0.707107,-0.707107;3.14159rad)
  sketch-geometry (4):
    g0: LineSegment StartX=0.463467 StartY=-5.33333 StartZ=0 EndX=0.463467 EndY=-8.33333 EndZ=0
    g1: LineSegment StartX=0.463467 StartY=-8.33333 StartZ=0 EndX=12.8699 EndY=-8.33333 EndZ=0
    g2: LineSegment StartX=12.8699 StartY=-8.33333 StartZ=0 EndX=12.8699 EndY=-5.33333 EndZ=0
    g3: LineSegment StartX=12.8699 StartY=-5.33333 StartZ=0 EndX=0.463467 EndY=-5.33333 EndZ=0
  constraints (12):
    c: Coincident(g0,g1)
    c: Coincident(g1,g2)
    c: Coincident(g2,g3)
    c: Coincident(g3,g0)
    c: Vertical(g0)
    c: Vertical(g2)
    c: Horizontal(g1)
    c: Horizontal(g3)
    c: DistanceX(g0,g-3) = 0.2032
    c: DistanceX(g-4,g1) = 0.2032
    c: Horizontal(g-3,g0)
    c: Horizontal(g-5,g0)
FEATURE [PartDesign::Pocket] Pocket004
  BaseFeature = -> Pocket003
  Direction = (0,1,2e-16)
  Length = 0
  Length2 = 5
  Placement = pos=(6.66667,21,-7.33333) rot=(0,0.707107,0.707107;3.14159rad)
  Profile = -> Sketch012
  ReferenceAxis = -> Sketch012 [N_Axis]
  Refine = true
  Suppressed = false
  Type = 3
  UpToFace = -> Pocket003 [Face18]
  UpToShape = -> [DatumPoint006]
FEATURE [Sketcher::SketchObject] Sketch013
  ArcFitTolerance = 1e-06
  AttachmentSupport = -> [DatumPlane004]
  ExternalGeometry = -> [DatumPoint008,DatumPoint010,DatumPoint009,Sketch008]
  FullyConstrained = false
  MakeInternals = false
  MapMode = 5
  Placement = pos=(0.362446,15,-0.177299) rot=(0,0.707107,0.707107;3.14159rad)
  sketch-geometry (3):
    g0: Circle [constr] CenterX=0.362446 CenterY=0.177299 CenterZ=0 NormalX=0 NormalY=0 NormalZ=1 AngleXU=0 Radius=1.625
    g1: Circle CenterX=0.362446 CenterY=0.177299 CenterZ=0 NormalX=0 NormalY=0 NormalZ=1 AngleXU=0 Radius=1.9426
    g2: LineSegment [constr] StartX=0.361977 StartY=2.1199 StartZ=0 EndX=0.361977 EndY=2.0183 EndZ=0
  constraints (8):
    c: PointOnObject(g-5,g0)
    c: PointOnObject(g-4,g0)
    c: PointOnObject(g-3,g0)
    c: Coincident(g1,g0)
    c: PointOnObject(g2,g1)
    c: Vertical(g2)
    c: PointOnObject(g2,g-6)
    c: Distance(g2,g2) = 0.1016
FEATURE [PartDesign::Pocket] Pocket005
  BaseFeature = -> Pocket004
  Direction = (0,-1,2e-16)
  Length = 5
  Length2 = 5
  Placement = pos=(6.66667,21,-7.33333) rot=(0,0.707107,0.707107;3.14159rad)
  Profile = -> Sketch013
  ReferenceAxis = -> Sketch013 [N_Axis]
  Refine = true
  Suppressed = false
  Type = 1
FEATURE [Sketcher::SketchObject] Sketch015
  ArcFitTolerance = 1e-06
  AttachmentSupport = -> [DatumPlane003]
  ExternalGeometry = -> [Binder003]
  FullyConstrained = true
  MakeInternals = false
  MapMode = 5
  Placement = pos=(6.50267,20.199,15.2607) rot=(1,0,0;1.5708rad)
  sketch-geometry (2):
    g0: LineSegment [constr] StartX=-12.4128 StartY=18.2897 StartZ=0 EndX=-27.6549 EndY=20.8214 EndZ=0
    g1: Circle CenterX=-20.0338 CenterY=19.5555 CenterZ=0 NormalX=0 NormalY=0 NormalZ=1 AngleXU=0 Radius=3.302
  constraints (4):
    c: Coincident(g0,g-5)
    c: Coincident(g0,g-3)
    c: Symmetric(g0,g0,g1)
    c: Diameter(g1) = 6.604
FEATURE [PartDesign::Pocket] Pocket006  label="dont press reset"
  BaseFeature = -> Pocket005
  Direction = (0,1,-2e-16)
  Length = 0
  Length2 = 5
  Offset = -0.762
  Placement = pos=(6.66667,21,-7.33333) rot=(0,0.707107,0.707107;3.14159rad)
  Profile = -> Sketch015
  ReferenceAxis = -> Sketch015 [N_Axis]
  Refine = true
  Suppressed = false
  Type = 3
  UpToFace = -> Pocket005 [Face13]
FEATURE [Sketcher::SketchObject] Sketch016
  ArcFitTolerance = 1e-06
  AttachmentSupport = -> [DatumPlane002]
  ExternalGeometry = -> [Binder003]
  FullyConstrained = true
  MakeInternals = false
  MapMode = 5
  Placement = pos=(6.66667,21,-7.33333) rot=(0,0.707107,0.707107;3.14159rad)
  sketch-geometry (2):
    g0: Circle CenterX=8.37978 CenterY=43.7214 CenterZ=0 NormalX=0 NormalY=0 NormalZ=1 AngleXU=0 Radius=1.778
    g1: Circle CenterX=-12.5794 CenterY=15.7794 CenterZ=0 NormalX=0 NormalY=0 NormalZ=1 AngleXU=0 Radius=1.778
  constraints (4):
    c: Coincident(g0,g-3)
    c: Coincident(g1,g-5)
    c: Equal(g0,g1)
    c: Diameter(g0) = 3.556
FEATURE [PartDesign::Plane] DatumPlane005
  AttachmentSupport = -> [Binder003]
  Length = 65.0694
  MapMode = 5
  Placement = pos=(0,17.278,0) rot=(0,0.707107,0.707107;3.14159rad)
  ResizeMode = 0
  Width = 79.6104
FEATURE [PartDesign::Pad] Pad009
  BaseFeature = -> Pocket006
  Direction = (0,1,-2e-16)
  Length = 10
  Length2 = 10
  Placement = pos=(6.66667,21,-7.33333) rot=(0,0.707107,0.707107;3.14159rad)
  Profile = -> Sketch016
  ReferenceAxis = -> Sketch016 [N_Axis]
  Refine = true
  Suppressed = false
  Type = 3
  UpToFace = -> DatumPlane005
FEATURE [Sketcher::SketchObject] Sketch017
  ArcFitTolerance = 1e-06
  AttachmentSupport = -> [DatumPlane005]
  ExternalGeometry = -> [Binder003]
  FullyConstrained = true
  MakeInternals = false
  MapMode = 5
  Placement = pos=(0,17.278,0) rot=(0,0.707107,0.707107;3.14159rad)
  sketch-geometry (2):
    g0: Circle CenterX=1.71311 CenterY=36.3881 CenterZ=0 NormalX=0 NormalY=0 NormalZ=1 AngleXU=0 Radius=1.21916
    g1: Circle CenterX=-19.246 CenterY=8.44604 CenterZ=0 NormalX=0 NormalY=0 NormalZ=1 AngleXU=0 Radius=1.21916
  constraints (4):
    c: Coincident(g0,g-3)
    c: Equal(g0,g-3)
    c: Coincident(g1,g-4)
    c: Equal(g1,g-4)
FEATURE [PartDesign::Pad] Pad010
  BaseFeature = -> Pad009
  Direction = (0,1,-2e-16)
  Length = 1.27
  Length2 = 10
  Placement = pos=(6.66667,21,-7.33333) rot=(0,0.707107,0.707107;3.14159rad)
  Profile = -> Sketch017
  ReferenceAxis = -> Sketch017 [N_Axis]
  Refine = true
  Reversed = true
  Suppressed = false
  TaperAngle = -20
  Type = 0
FEATURE [PartDesign::Body] Body002
  AllowCompound = false
  Group = -> [DatumPlane002,Sketch004,DatumPoint,DatumPoint001,DatumPoint002,DatumPoint003,DatumPoint004,DatumPoint005,Pad003,Binder002,Sketch005,DatumPlane003,Pad004,Sketch006,Sketch014,Pad008,Pad005,Sketch008,Pad006,Sketch007,Sketch011,Binder003,Pocket003,DatumPoint006,DatumPoint007,Sketch012,Pocket004,DatumPlane004,DatumPoint008,DatumPoint009,DatumPoint010,Sketch013,Pocket005,Sketch015,Pocket006,Sketch016,+4 more]
  Origin = -> Origin005
  Tip = -> Pad010
FEATURE [App::Part] Part  label="sensor enclosure"
  Group = -> [Body001,Body002]
  Origin = -> Origin
